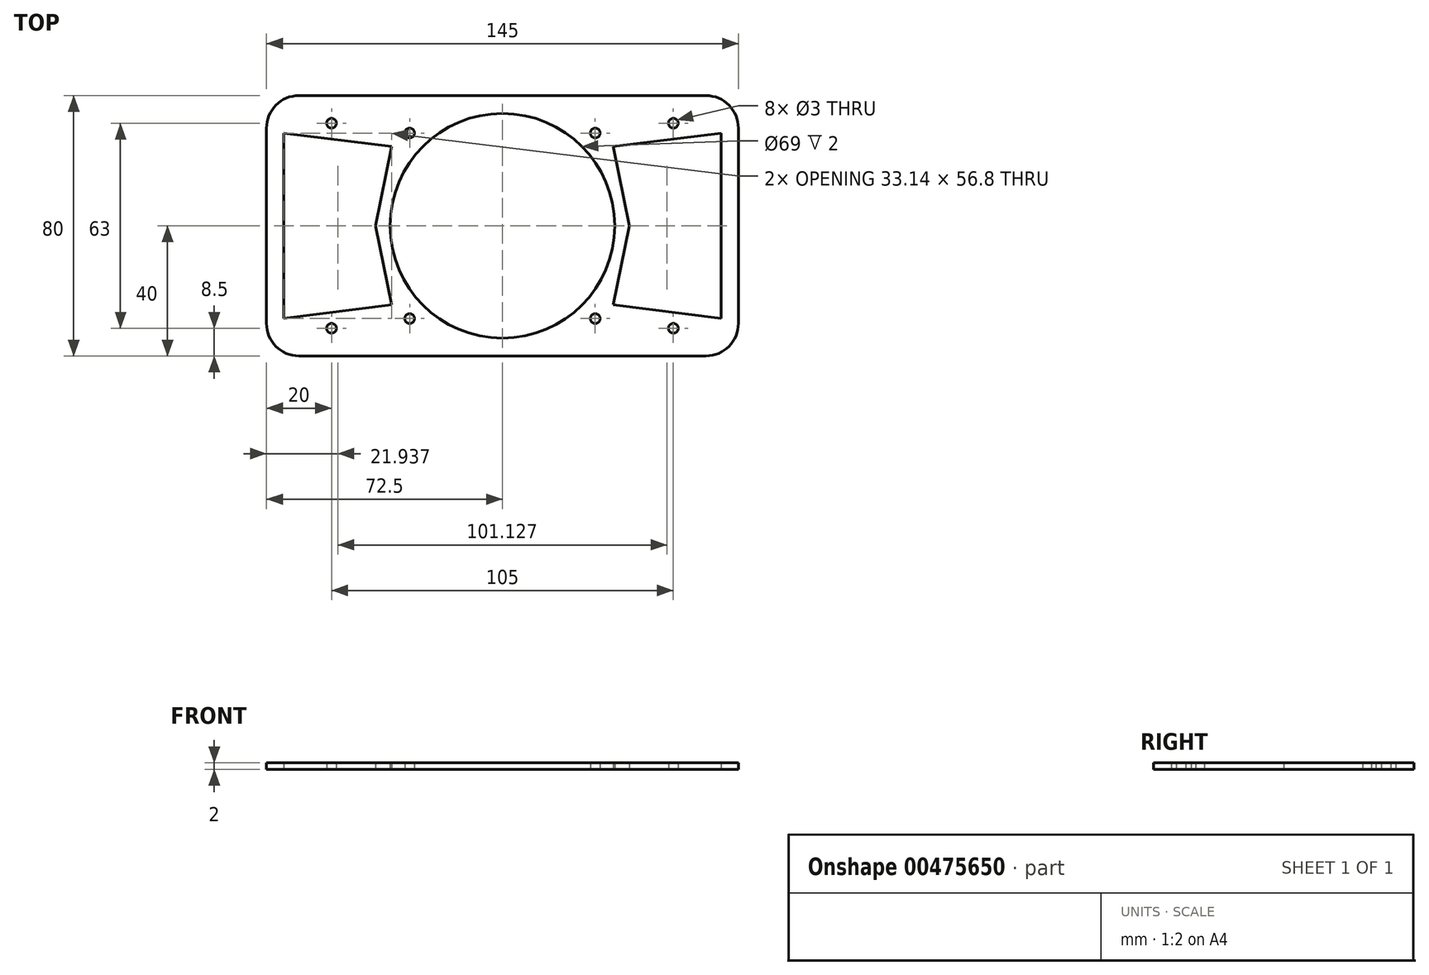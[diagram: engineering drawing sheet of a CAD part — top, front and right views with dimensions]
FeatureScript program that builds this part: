
annotation { "Feature Type Name" : "Feature", "Feature Type Description" : "" }
export const myFeature = defineFeature(function(context is Context, id is Id, definition is map)
    precondition{}
    {
        {
            var Q0;
            Q0=qCreatedBy(makeId("Top.planeOp"),FACE);
            var sketch = newSketch(context, id + "F0", { "sketchPlane" : qUnion([Q0])});
            skLineSegment(sketch, "E0.bottom", {"start": v(-72.5, 40) * mm, "end": v(72.5, 40) * mm});
            skLineSegment(sketch, "E0.top", {"start": v(-72.5, -40) * mm, "end": v(72.5, -40) * mm});
            skLineSegment(sketch, "E0.left", {"start": v(-72.5, 40) * mm, "end": v(-72.5, -40) * mm});
            skLineSegment(sketch, "E0.right", {"start": v(72.5, 40) * mm, "end": v(72.5, -40) * mm});
            skPoint(sketch, "E0.middle", {"position": v(0, 0) * mm});
            skLineSegment(sketch, "E1.bottom", {"start": v(-52.5, 31.5) * mm, "end": v(52.5, 31.5) * mm, "construction": true});
            skLineSegment(sketch, "E1.top", {"start": v(-52.5, -31.5) * mm, "end": v(52.5, -31.5) * mm, "construction": true});
            skLineSegment(sketch, "E1.left", {"start": v(-52.5, 31.5) * mm, "end": v(-52.5, -31.5) * mm, "construction": true});
            skLineSegment(sketch, "E1.right", {"start": v(52.5, 31.5) * mm, "end": v(52.5, -31.5) * mm, "construction": true});
            skLineSegment(sketch, "E2.bottom", {"start": v(-28.5, 28.5) * mm, "end": v(28.5, 28.5) * mm, "construction": true});
            skLineSegment(sketch, "E2.top", {"start": v(-28.5, -28.5) * mm, "end": v(28.5, -28.5) * mm, "construction": true});
            skLineSegment(sketch, "E2.left", {"start": v(-28.5, 28.5) * mm, "end": v(-28.5, -28.5) * mm, "construction": true});
            skLineSegment(sketch, "E2.right", {"start": v(28.5, 28.5) * mm, "end": v(28.5, -28.5) * mm, "construction": true});
            skCircle(sketch, "E3", {"center": v(-52.5, 31.5) * mm, "radius": 1.5 * mm});
            skCircle(sketch, "E4", {"center": v(52.5, 31.5) * mm, "radius": 1.5 * mm});
            skCircle(sketch, "E5", {"center": v(52.5, -31.5) * mm, "radius": 1.5 * mm});
            skCircle(sketch, "E6", {"center": v(-52.5, -31.5) * mm, "radius": 1.5 * mm});
            skCircle(sketch, "E7", {"center": v(-28.5, 28.5) * mm, "radius": 1.5 * mm});
            skCircle(sketch, "E8", {"center": v(28.5, 28.5) * mm, "radius": 1.5 * mm});
            skCircle(sketch, "E9", {"center": v(28.5, -28.5) * mm, "radius": 1.5 * mm});
            skCircle(sketch, "E10", {"center": v(-28.5, -28.5) * mm, "radius": 1.5 * mm});
            skCircle(sketch, "E11", {"center": v(0, 0) * mm, "radius": 34.5 * mm});
            skLineSegment(sketch, "E12", {"start": v(38.94, 0) * mm, "end": v(34, 24.31) * mm});
            skLineSegment(sketch, "E13", {"start": v(34, 24.31) * mm, "end": v(67.13, 28.4) * mm});
            skLineSegment(sketch, "E14", {"start": v(67.13, 28.4) * mm, "end": v(67.13, 0) * mm});
            skLineSegment(sketch, "E15.MirrorCS", {"start": v(38.94, 0) * mm, "end": v(34, -24.31) * mm});
            skLineSegment(sketch, "E16.MirrorCS", {"start": v(34, -24.31) * mm, "end": v(67.13, -28.4) * mm});
            skLineSegment(sketch, "E17.MirrorCS", {"start": v(67.13, -28.4) * mm, "end": v(67.13, 0) * mm});
            skLineSegment(sketch, "E18.MirrorCS", {"start": v(-34, 24.31) * mm, "end": v(-67.13, 28.4) * mm});
            skLineSegment(sketch, "E19.MirrorCS", {"start": v(-67.13, 28.4) * mm, "end": v(-67.13, 0) * mm});
            skLineSegment(sketch, "E20.MirrorCS", {"start": v(-67.13, -28.4) * mm, "end": v(-67.13, 0) * mm});
            skLineSegment(sketch, "E21.MirrorCS", {"start": v(-34, -24.31) * mm, "end": v(-67.13, -28.4) * mm});
            skLineSegment(sketch, "E22.MirrorCS", {"start": v(-38.94, 0) * mm, "end": v(-34, -24.31) * mm});
            skLineSegment(sketch, "E23.MirrorCS", {"start": v(-38.94, 0) * mm, "end": v(-34, 24.31) * mm});
            skSolve(sketch);
        }
        {
            var Q0;
            Q0=makeQuery(id+"F0.imprint","IMPRINT",FACE,{"disambiguationData":[TD([[makeQuery(id+"F0.imprint","IMPRINT",EDGE,{"derivedFrom":sQuery(id+"F0.wireOp",EDGE,"E0.bottom")}),-1.0]])]});
            extrude(context, id + "F1", {"entities" : qUnion([Q0]), "depth" : 2 * mm});
        }
        {
            var Q0;
            Q0=makeQuery(id+"F1.opExtrude","SWEPT_EDGE",EDGE,{"disambiguationData":[OSD([sQuery(id+"F0.wireOp",EDGE,"E0.bottom"),sQuery(id+"F0.wireOp",EDGE,"E0.left")])]});
            var Q1;
            Q1=makeQuery(id+"F1.opExtrude","SWEPT_EDGE",EDGE,{"disambiguationData":[OSD([sQuery(id+"F0.wireOp",EDGE,"E0.bottom"),sQuery(id+"F0.wireOp",EDGE,"E0.right")])]});
            var Q2;
            Q2=makeQuery(id+"F1.opExtrude","SWEPT_EDGE",EDGE,{"disambiguationData":[OSD([sQuery(id+"F0.wireOp",EDGE,"E0.top"),sQuery(id+"F0.wireOp",EDGE,"E0.right")])]});
            var Q3;
            Q3=makeQuery(id+"F1.opExtrude","SWEPT_EDGE",EDGE,{"disambiguationData":[OSD([sQuery(id+"F0.wireOp",EDGE,"E0.top"),sQuery(id+"F0.wireOp",EDGE,"E0.left")])]});
            fillet(context, id + "F2", {"entities" : qUnion([Q0, Q1, Q2, Q3]), "radius" : 10 * mm, "tangentPropagation" : true, "allowEdgeOverflow" : false});
        }
    });
